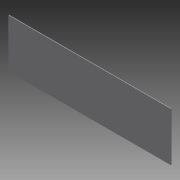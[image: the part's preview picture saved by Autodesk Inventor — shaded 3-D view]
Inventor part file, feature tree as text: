
AUTODESK INVENTOR PART (.ipt)
format: ipt  version: 2012 (Build 160160000, 160)  size: 66,048 bytes
history: native  units: in
note: dims shown in document units (in); Inventor stores cm internally (conversion verified against a paired STEP export)
features: extrude x1, sketch x1
ambient origin geometry x8: Origin, YZ Plane, XZ Plane, XY Plane, X Axis, Y Axis, Z Axis, Center Point
bodies: Solid1 (feature_tree)
feature tree (2):
  extrude  "Extrusion1"  Depth=2.5in
  sketch  "Sketch1"  dims[d0=0.75in d1=2.5in d2=0.01in d3=0.0in]
